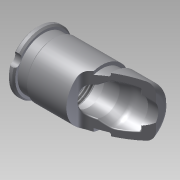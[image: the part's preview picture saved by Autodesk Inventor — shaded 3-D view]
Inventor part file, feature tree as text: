
AUTODESK INVENTOR PART (.ipt)
format: ipt  version: 2011 SP1 (Build 150282100, 282)  size: 359,936 bytes
history: native  units: mm
features: sketch x4, other x3, extrude x3, fillet x3, revolve x1, thread x1
ambient origin geometry x8: Origin, YZ Plane, XZ Plane, XY Plane, X Axis, Y Axis, Z Axis, Center Point
feature tree (15):
  other  "Твердое тело1"
  revolve  "Вращение1"
  extrude  "Выдавливание1"  Depth=4.0mm
  fillet  "Сопряжение3"  Radius=7.05mm
  fillet  "Сопряжение1"  Radius=4.363323mm
  extrude  "Выдавливание2"  Depth=5.0mm
  fillet  "Сопряжение4"  Radius=16.3mm
  extrude  "Выдавливание3"  Depth=7.0mm
  thread  "Резьба1"
  sketch  "Эскиз1"
  sketch  "Эскиз2"
  sketch  "Эскиз3"
  sketch  "Эскиз4"
  other  "Проецирование ребер1"
  other  "Проецирование ребер2"
